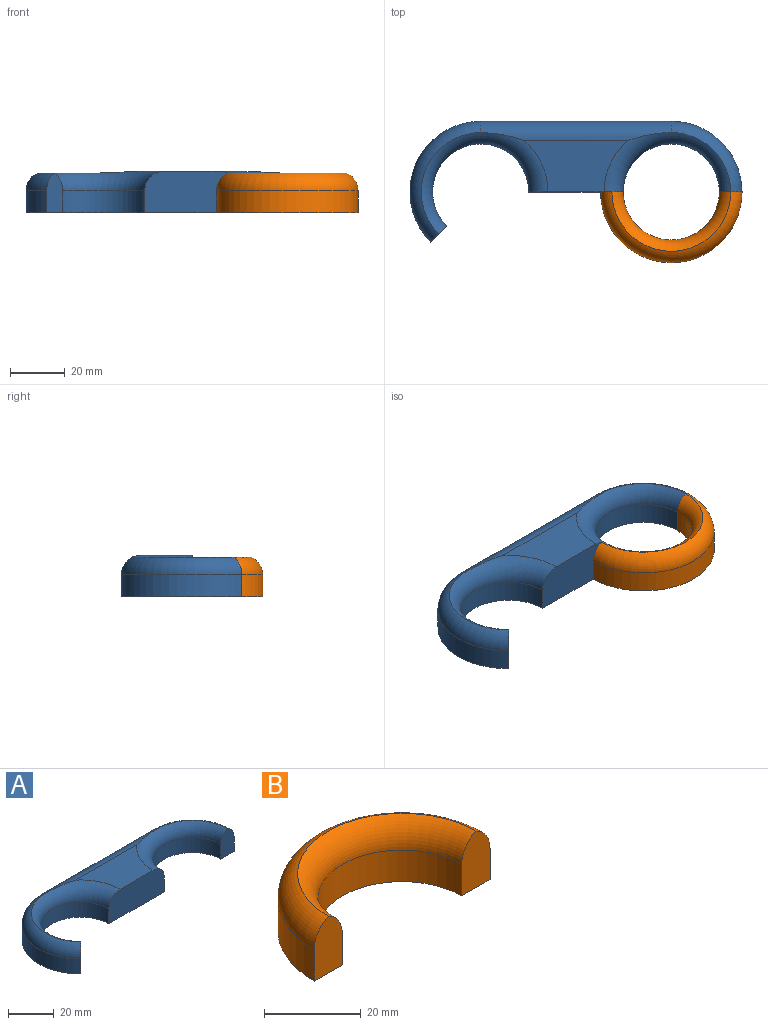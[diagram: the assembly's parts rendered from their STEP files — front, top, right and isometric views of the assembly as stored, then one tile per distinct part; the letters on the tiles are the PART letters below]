
ASSEMBLY  parts=2 mates=1
PART A: 15 faces, bbox 133.1x54.4x15 mm
  f0: cylinder r=17.48mm len=34.97mm, axis (0,0,-1), area 549.3mm2, adj f1,f7,f9,f12
  f1: plane 34.41x15mm, normal (0,-1,0), area 495.2mm2, adj f0,f2,f8,f9,f11,f12
  f2: cylinder r=17.48mm len=34.97mm, axis (0,0,-1), area 439.4mm2, adj f1,f3,f9,f11
  f3: plane 14.38x8.25mm, normal (0,-1,0), area 103.9mm2, adj f2,f4,f9,f10,f11
  f4: cylinder r=25.73mm len=25.73mm, axis (0,0,-1), area 323.4mm2, adj f3,f5,f9,f10
  f5: plane 69.38x8mm, normal (0,1,0), area 555mm2, adj f4,f6,f9,f13
  f6: cylinder r=25.73mm len=43.93mm, axis (0,0,-1), area 485.1mm2, adj f5,f7,f9,f14
  f7: plane 14.38x5.83mm, normal (0.71,-0.71,0), area 103.9mm2, adj f0,f6,f9,f12,f14
  f8: plane 37.85x18.73mm, normal (0,0,1), area 482.1mm2, adj f1,f11,f12,f13
  f9: plane 120.85x43.93mm, normal (0,0,-1), area 2005.3mm2, adj f0,f1,f2,f3,f4,f5,f6,f7
  f10: torus R=18.73mm, axis (0,0,1), area 306.6mm2, adj f3,f4,f11,f13
  f11: torus R=24.48mm, axis (0,0,1), area 552.2mm2, adj f1,f2,f3,f8,f10,f13
  f12: torus R=24.48mm, axis (0,0,1), area 671.6mm2, adj f0,f1,f7,f8,f13,f14
  f13: cylinder r=7mm len=69.38mm, axis (1,0,0), area 701.2mm2, adj f5,f8,f10,f11,f12,f14
  f14: torus R=18.73mm, axis (0,0,1), area 459.8mm2, adj f6,f7,f12,f13
PART B: 7 faces, bbox 55.7x27.9x15 mm
  f0: plane 14.38x8.25mm, normal (0,-1,0), area 103.9mm2, adj f1,f3,f4,f5,f6
  f1: cylinder r=17.48mm len=34.97mm, axis (0,0,-1), area 439.4mm2, adj f0,f2,f4,f6
  f2: plane 14.38x8.25mm, normal (0,-1,0), area 103.9mm2, adj f1,f3,f4,f5,f6
  f3: cylinder r=25.73mm len=51.47mm, axis (0,0,-1), area 646.8mm2, adj f0,f2,f4,f5
  f4: plane 51.47x25.73mm, normal (0,0,-1), area 560.1mm2, adj f0,f1,f2,f3
  f5: torus R=18.73mm, axis (0,0,1), area 613.1mm2, adj f0,f2,f3,f6
  f6: torus R=24.48mm, axis (0,0,1), area 477.5mm2, adj f0,f1,f2,f5
PLACE A t=(5.7,-20.37,-17.24)mm
PLACE B rot(axis=(0,0,-1),180deg) t=(5.7,-20.37,-17.24)mm
MATE fastened A.f3 <-> B.f0  axis (0,-1,0) through (27.31,-20.37,-10.86)mm
